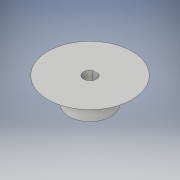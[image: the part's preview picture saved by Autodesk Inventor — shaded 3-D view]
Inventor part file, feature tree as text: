
AUTODESK INVENTOR PART (.ipt)
format: ipt  version: 2019 (Build 230136000, 136)  size: 129,024 bytes
history: native  units: in
note: dims shown in document units (in); Inventor stores cm internally (conversion verified against a paired STEP export)
features: sketch x2, other x1, revolve x1, extrude x1
ambient origin geometry x8: Origin, YZ Plane, XZ Plane, XY Plane, X Axis, Y Axis, Z Axis, Center Point
bodies: Body1 (feature_tree)
feature tree (5):
  other  "spool"
  revolve  "Revolution1"  [1 undecoded]
  extrude  "Extrusion1"  TaperAngle=90.0deg  [1 undecoded]
  sketch  "Sketch4"  dims[d18=0.375in d19=0.45in]
  sketch  "Sketch5"  dims[d20=0.75in d21=90.0deg d22=0.23in d23=0.101in d24=1.0in d25=0.0in]
note: 2 required parameter values undecoded (feature->parameter linkage not recoverable at this tier; creation-order binding heuristic only, values carry confidence <= 0.55)